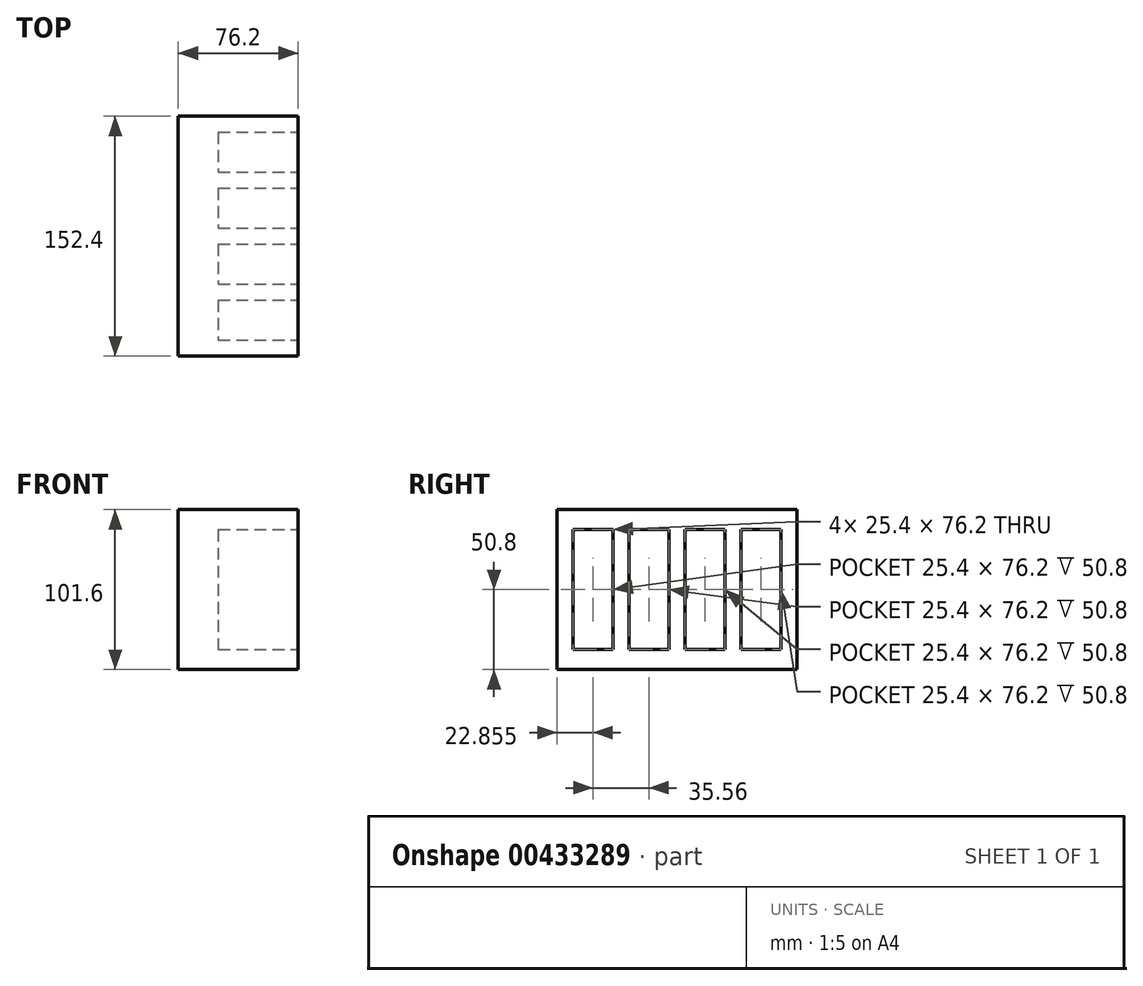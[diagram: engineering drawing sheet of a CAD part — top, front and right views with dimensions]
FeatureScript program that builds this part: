
annotation { "Feature Type Name" : "Feature", "Feature Type Description" : "" }
export const myFeature = defineFeature(function(context is Context, id is Id, definition is map)
    precondition{}
    {
        {
            var Q0;
            Q0=qCreatedBy(makeId("Top.planeOp"),FACE);
            var sketch = newSketch(context, id + "F0", { "sketchPlane" : qUnion([Q0])});
            skLineSegment(sketch, "E0.bottom", {"start": v(-37.27, 110.33) * mm, "end": v(38.93, 110.33) * mm});
            skLineSegment(sketch, "E0.top", {"start": v(-37.27, -42.07) * mm, "end": v(38.93, -42.07) * mm});
            skLineSegment(sketch, "E0.left", {"start": v(-37.27, 110.33) * mm, "end": v(-37.27, -42.07) * mm});
            skLineSegment(sketch, "E0.right", {"start": v(38.93, 110.33) * mm, "end": v(38.93, -42.07) * mm});
            skSolve(sketch);
        }
        {
            var Q0;
            Q0=makeQuery(id+"F0.imprint","IMPRINT",FACE,{"disambiguationData":[TD([[makeQuery(id+"F0.imprint","IMPRINT",EDGE,{"derivedFrom":sQuery(id+"F0.wireOp",EDGE,"E0.bottom")}),-1.0]])]});
            extrude(context, id + "F1", {"entities" : qUnion([Q0]), "depth" : 101.6 * mm});
        }
        {
            var Q0;
            Q0=makeQuery(id+"F1.opExtrude","SWEPT_FACE",FACE,{"disambiguationData":[OSD([sQuery(id+"F0.wireOp",EDGE,"E0.right")])]});
            var sketch = newSketch(context, id + "F2", { "sketchPlane" : qUnion([Q0])});
            skLineSegment(sketch, "E1.bottom", {"start": v(100.17, 88.9) * mm, "end": v(74.77, 88.9) * mm});
            skLineSegment(sketch, "E1.top", {"start": v(100.17, 12.7) * mm, "end": v(74.77, 12.7) * mm});
            skLineSegment(sketch, "E1.left", {"start": v(100.17, 88.9) * mm, "end": v(100.17, 12.7) * mm});
            skLineSegment(sketch, "E1.right", {"start": v(74.77, 88.9) * mm, "end": v(74.77, 12.7) * mm});
            skLineSegment(sketch, "E2.1.0.0", {"start": v(64.6, 88.9) * mm, "end": v(39.2, 88.9) * mm});
            skLineSegment(sketch, "E2.1.0.1", {"start": v(64.6, 88.9) * mm, "end": v(64.6, 12.7) * mm});
            skLineSegment(sketch, "E2.1.0.2", {"start": v(39.2, 88.9) * mm, "end": v(39.2, 12.7) * mm});
            skLineSegment(sketch, "E2.1.0.3", {"start": v(64.6, 12.7) * mm, "end": v(39.2, 12.7) * mm});
            skLineSegment(sketch, "E2.2.0.0", {"start": v(29.05, 88.9) * mm, "end": v(3.65, 88.9) * mm});
            skLineSegment(sketch, "E2.2.0.1", {"start": v(29.05, 88.9) * mm, "end": v(29.05, 12.7) * mm});
            skLineSegment(sketch, "E2.2.0.2", {"start": v(3.65, 88.9) * mm, "end": v(3.65, 12.7) * mm});
            skLineSegment(sketch, "E2.2.0.3", {"start": v(29.05, 12.7) * mm, "end": v(3.65, 12.7) * mm});
            skLineSegment(sketch, "E2.3.0.0", {"start": v(-6.51, 88.9) * mm, "end": v(-31.91, 88.9) * mm});
            skLineSegment(sketch, "E2.3.0.1", {"start": v(-6.51, 88.9) * mm, "end": v(-6.51, 12.7) * mm});
            skLineSegment(sketch, "E2.3.0.2", {"start": v(-31.91, 88.9) * mm, "end": v(-31.91, 12.7) * mm});
            skLineSegment(sketch, "E2.3.0.3", {"start": v(-6.51, 12.7) * mm, "end": v(-31.91, 12.7) * mm});
            skLineSegment(sketch, "E2.direction1", {"start": v(74.77, 88.9) * mm, "end": v(39.2, 88.9) * mm, "construction": true});
            skSolve(sketch);
        }
        {
            var Q0;
            Q0=makeQuery(id+"F2.imprint","IMPRINT",FACE,{"disambiguationData":[TD([[makeQuery(id+"F2.imprint","IMPRINT",EDGE,{"derivedFrom":sQuery(id+"F2.wireOp",EDGE,"E1.bottom")}),1.0]])]});
            var Q1;
            Q1=makeQuery(id+"F2.imprint","IMPRINT",FACE,{"disambiguationData":[TD([[makeQuery(id+"F2.imprint","IMPRINT",EDGE,{"derivedFrom":sQuery(id+"F2.wireOp",EDGE,"E2.1.0.0")}),1.0]])]});
            var Q2;
            Q2=makeQuery(id+"F2.imprint","IMPRINT",FACE,{"disambiguationData":[TD([[makeQuery(id+"F2.imprint","IMPRINT",EDGE,{"derivedFrom":sQuery(id+"F2.wireOp",EDGE,"E2.2.0.0")}),1.0]])]});
            var Q3;
            Q3=makeQuery(id+"F2.imprint","IMPRINT",FACE,{"disambiguationData":[TD([[makeQuery(id+"F2.imprint","IMPRINT",EDGE,{"derivedFrom":sQuery(id+"F2.wireOp",EDGE,"E2.3.0.0")}),1.0]])]});
            extrude(context, id + "F3", {"entities" : qUnion([Q0, Q1, Q2, Q3]), "operationType" : NewBodyOperationType.REMOVE, "oppositeDirection" : true, "depth" : 50.8 * mm});
        }
    });
